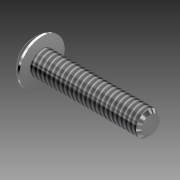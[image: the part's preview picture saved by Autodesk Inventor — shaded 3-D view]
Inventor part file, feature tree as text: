
AUTODESK INVENTOR PART (.ipt)
format: ipt  version: 2011 (Build 150239000, 239)  size: 113,664 bytes
history: native  units: in
note: dims shown in document units (in); Inventor stores cm internally (conversion verified against a paired STEP export)
features: other x1, imported_body x1, thread x1
ambient origin geometry x8: Origin, YZ Plane, XZ Plane, XY Plane, X Axis, Y Axis, Z Axis, Center Point
feature tree (3):
  parser-record x1  (decoder bookkeeping rows leaked as tree rows — omitted from the tree; the rows remain in map.json)
  imported_body  "Base1"
  thread  "Thread1"  [1 undecoded]
note: 1 required parameter value undecoded (feature->parameter linkage not recoverable at this tier; creation-order binding heuristic only, values carry confidence <= 0.55)
